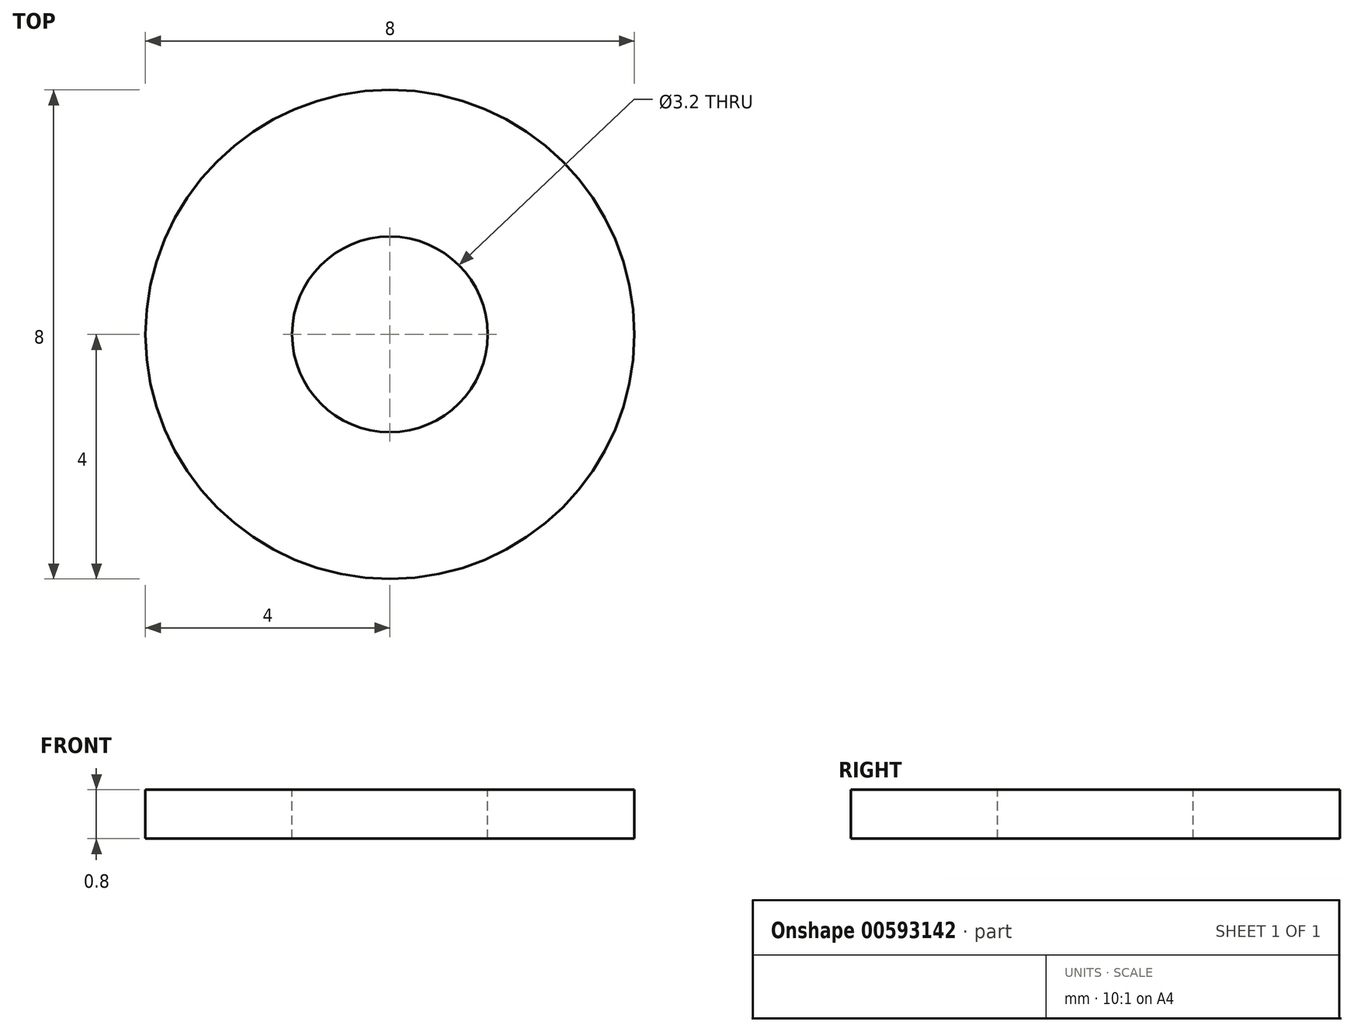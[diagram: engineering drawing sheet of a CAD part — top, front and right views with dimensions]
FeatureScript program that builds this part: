
annotation { "Feature Type Name" : "Feature", "Feature Type Description" : "" }
export const myFeature = defineFeature(function(context is Context, id is Id, definition is map)
    precondition{}
    {
        {
            var Q0;
            Q0=qCreatedBy(makeId("Top.planeOp"),FACE);
            var sketch = newSketch(context, id + "F0", { "sketchPlane" : qUnion([Q0])});
            skCircle(sketch, "E0", {"center": v(0, 0) * mm, "radius": 4 * mm});
            skSolve(sketch);
        }
        {
            var Q0;
            Q0 = qSketchRegion(id + "F0", true);
            extrude(context, id + "F1", {"entities" : qUnion([Q0]), "endBound" : BoundingType.SYMMETRIC, "depth" : 0.8 * mm, "offsetDistance" : 25 * mm});
        }
        {
            var Q0;
            Q0=makeQuery(id+"F1.opExtrude","CAP_FACE",FACE,{"disambiguationData":[OSD([sQuery(id+"F0.wireOp",EDGE,"E0")])],"isStart":false});
            var sketch = newSketch(context, id + "F2", { "sketchPlane" : qUnion([Q0])});
            skPoint(sketch, "E1", {"position": v(0, 0) * mm});
            skSolve(sketch);
        }
        {
            var Q0;
            Q0=sQuery(id+"F2.wireOp",VERTEX,"E1");
            var Q1;
            Q1=makeQuery(id+"F1.opExtrude","SWEPT_BODY",BODY,{"disambiguationData":[OSD([sQuery(id+"F0.wireOp",EDGE,"E0")])]});
            hole(context, id + "F3", {"style" : HoleStyle.SIMPLE, "endStyle" : HoleEndStyle.THROUGH, "holeDiameter" : 3.2 * mm, "majorDiameter" : 5 * mm, "isTappedThrough" : true, "tappedDepth" : 12 * mm, "tapClearance" : 3, "startFromSketch" : true, "locations" : qUnion([Q0]), "scope" : qUnion([Q1])});
        }
    });
